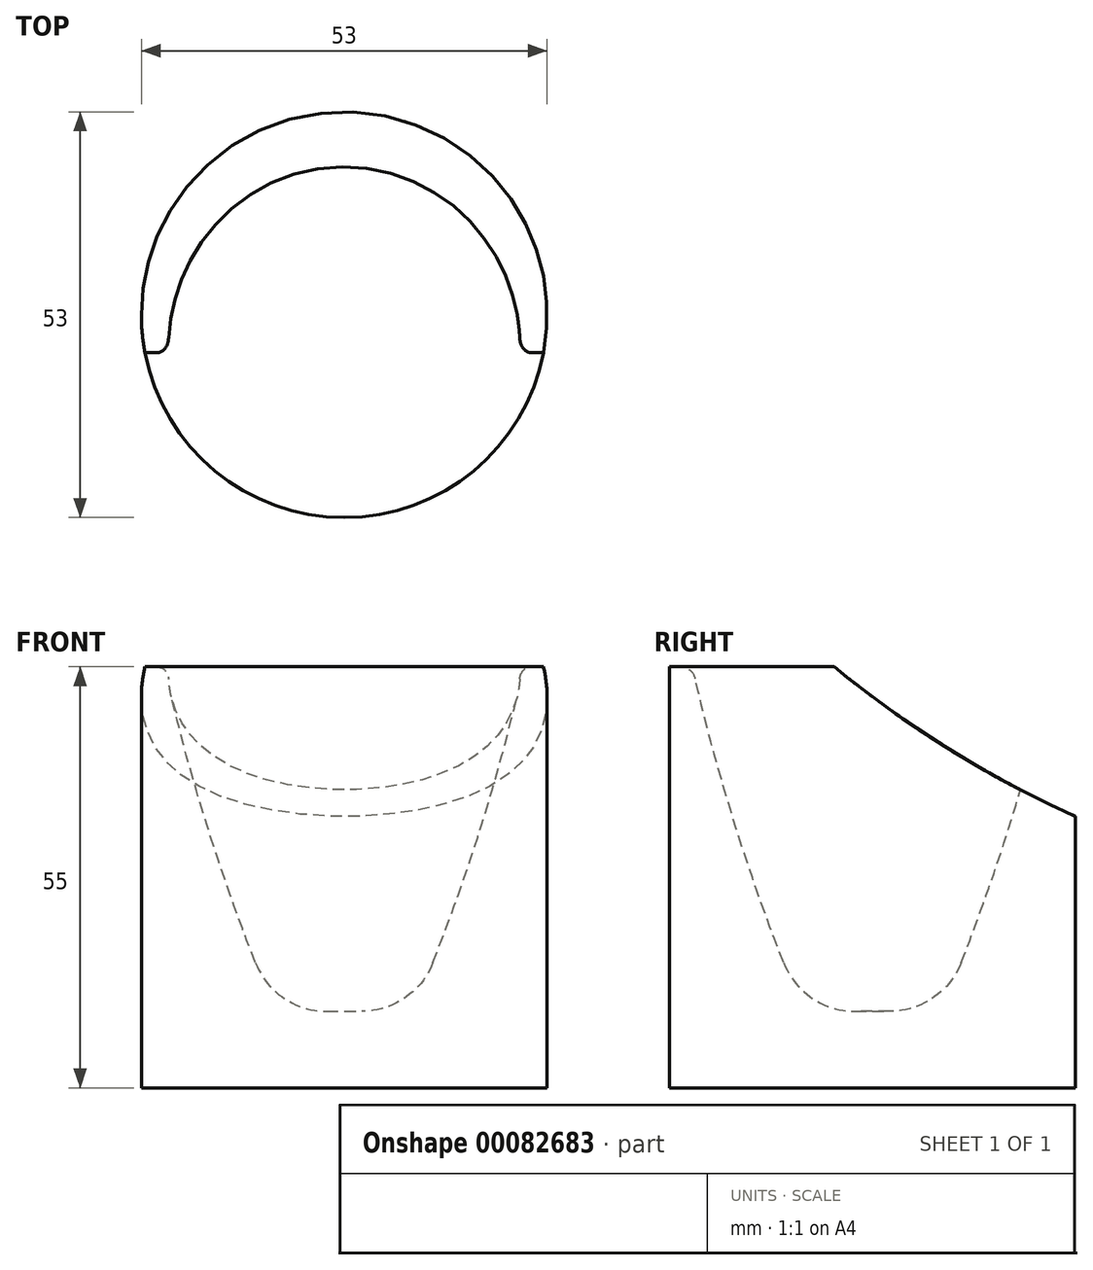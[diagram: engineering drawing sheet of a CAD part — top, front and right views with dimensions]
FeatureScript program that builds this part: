
annotation { "Feature Type Name" : "Feature", "Feature Type Description" : "" }
export const myFeature = defineFeature(function(context is Context, id is Id, definition is map)
    precondition{}
    {
        {
            var Q0;
            Q0=qCreatedBy(makeId("Front.planeOp"),FACE);
            var sketch = newSketch(context, id + "F0", { "sketchPlane" : qUnion([Q0])});
            skLineSegment(sketch, "E0.bottom", {"start": v(0, 0) * mm, "end": v(26.5, 0) * mm});
            skLineSegment(sketch, "E0.top", {"start": v(23.5, 55) * mm, "end": v(26.5, 55) * mm});
            skLineSegment(sketch, "E0.right", {"start": v(26.5, 0) * mm, "end": v(26.5, 55) * mm});
            skLineSegment(sketch, "E1", {"start": v(26.5, 55) * mm, "end": v(25.1, 55) * mm});
            skLineSegment(sketch, "E2", {"start": v(0, 10) * mm, "end": v(9, 10) * mm});
            skArc(sketch, "E3", {"start": v(9, 10) * mm, "mid": v(17, 31.42) * mm, "end": v(23.14, 53.45) * mm});
            skLineSegment(sketch, "E4", {"start": v(0, -16.75) * mm, "end": v(0, -16.75) * mm});
            skPoint(sketch, "E4.endSnap0", {"position": v(0, 5) * mm});
            skLineSegment(sketch, "E5", {"start": v(0, 0) * mm, "end": v(0, 10) * mm});
            skLineSegment(sketch, "E6", {"start": v(0, -16.75) * mm, "end": v(0, 51.32) * mm, "construction": true});
            skPoint(sketch, "E7.visualSharp", {"position": v(23.5, 55) * mm});
            skArc(sketch, "E7.filletArc", {"start": v(25.1, 55) * mm, "mid": v(23.85, 54.57) * mm, "end": v(23.14, 53.45) * mm});
            skSolve(sketch);
        }
        {
            var Q0;
            Q0=makeQuery(id+"F0.imprint","IMPRINT",FACE,{"disambiguationData":[TD([[makeQuery(id+"F0.imprint","IMPRINT",EDGE,{"derivedFrom":sQuery(id+"F0.wireOp",EDGE,"E0.bottom")}),1.0]])]});
            var Q1;
            Q1=sQuery(id+"F0.wireOp",EDGE,"E6");
            revolve(context, id + "F1", {"entities" : qUnion([Q0]), "axis" : qUnion([Q1]), "revolveType" : RevolveType.FULL});
        }
        {
            var Q0;
            Q0=qCreatedBy(makeId("Right.planeOp"),FACE);
            var sketch = newSketch(context, id + "F2", { "sketchPlane" : qUnion([Q0])});
            skLineSegment(sketch, "E8.0", {"start": v(26.5, 55) * mm, "end": v(-26.5, 55) * mm});
            skLineSegment(sketch, "E9.0", {"start": v(26.5, 0) * mm, "end": v(-26.5, 0) * mm});
            skCircle(sketch, "E10", {"center": v(84.2, 163.6) * mm, "radius": 140.52 * mm});
            skPoint(sketch, "E10.first.point", {"position": v(-4.98, 55) * mm});
            skPoint(sketch, "E10.second.point", {"position": v(61.03, 25) * mm});
            skPoint(sketch, "E10.third.point", {"position": v(220.03, 127.6) * mm});
            skLineSegment(sketch, "E11", {"start": v(-4.98, -8.98) * mm, "end": v(-4.98, 66.57) * mm, "construction": true});
            skSolve(sketch);
        }
        {
            var Q0;
            Q0=makeQuery(id+"F2.imprint","IMPRINT",FACE,{"disambiguationData":[TD([[makeQuery(id+"F2.imprint","IMPRINT",EDGE,{"derivedFrom":sQuery(id+"F2.wireOp",EDGE,"E10")}),1.0]])]});
            extrude(context, id + "F3", {"entities" : qUnion([Q0]), "operationType" : NewBodyOperationType.REMOVE, "endBound" : BoundingType.SYMMETRIC, "oppositeDirection" : true, "depth" : 105.64 * mm});
        }
        {
            var Q0;
            Q0=makeQuery(id+"F1.opRevolve","SWEPT_EDGE",EDGE,{"disambiguationData":[OSD([sQuery(id+"F0.wireOp",EDGE,"E2"),sQuery(id+"F0.wireOp",EDGE,"E3")])]});
            fillet(context, id + "F4", {"entities" : qUnion([Q0]), "radius" : 10 * mm, "tangentPropagation" : true, "allowEdgeOverflow" : false});
        }
    });
